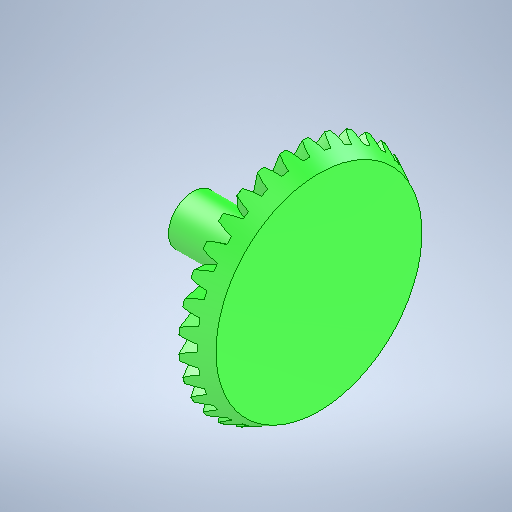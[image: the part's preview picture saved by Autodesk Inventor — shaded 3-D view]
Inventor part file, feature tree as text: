
AUTODESK INVENTOR PART (.ipt)
format: ipt  version: 2025.1 (Build 291241000, 241)  size: 666,624 bytes
history: native  units: in
note: dims shown in document units (in); Inventor stores cm internally (conversion verified against a paired STEP export)
features: sketch x8, extrude x5, plane x3, pattern_circular x3, revolve x1, hole x1, fillet x1, other x1
ambient origin geometry x8: Origin, YZ Plane, XZ Plane, XY Plane, X Axis, Y Axis, Z Axis, Center Point
bodies: Solid1 (feature_tree)
feature tree (23):
  revolve  "Revolution1"  [1 undecoded]
  plane  "Work Plane7"
  extrude  "Extrusion7"  Depth=0.0945in
  plane  "Work Plane8"
  sketch  "Sketch13"  dims[d5=0.3937in d9=1.5748in]
  extrude  "Extrusion9"  Depth=0.3937in
  pattern_circular  "Circular Pattern4"  [2 undecoded]
  pattern_circular  "Circular Pattern5"  [2 undecoded]
  extrude  "Extrusion10"  Depth=0.0394in
  extrude  "Extrusion11"  Depth=0.0394in
  extrude  "Extrusion12"  Depth=0.0394in
  pattern_circular  "Circular Pattern6"  [2 undecoded]
  hole  "Perçage1"  [1 undecoded]
  fillet  "Congé3"  Radius=0.0945in
  sketch  "Sketch1"  dims[d0=3.1496in d1=0.1825in]
  plane  "Work Plane6"
  sketch  "Sketch11"  dims[d2=0.0787in d3=0.0945in]
  sketch  "Sketch14"  dims[d10=90.0deg]
  sketch  "Sketch15"  dims[d74=0.4359in]
  sketch  "Sketch16"  dims[d75=0.7087in]
  sketch  "Sketch18"  dims[d76=0.9449in d77=1.4085in d78=0.7043in d86=-0.1825in d87=1.5748in d88=0.0691in d89=0.1374in d90=0.0787in d91=0.0197in d92=0.0945in d93=0.0079in d94=0.0079in d95=0.4724in d96=-0.0197in d109=0.2406in d110=-0.2406in d111=2.8171in d112=1.3386in d113=0.4724in d114=0.5906in d115=0.0in d116=2.3622in d117=360.0deg d119=12.5984in d120=360.0deg d122=1.1811in d123=0.0787in d124=0.0in d125=0.6142in d126=1.2598in d127=0.0in d128=0.1969in d129=0.7874in d130=0.2362in d131=0.0in d132=1.5748in d133=360.0deg d136=0.1181in d137=0.2362in d138=0.119in d139=0.0787in d140=0.5635in d141=0.2362in d142=0.8108in d143=0.1476in d144=0.0787in d145=0.7874in d147=360.0deg d149=0.0394in]
  sketch  "Esquisse19"
  other  "Réseau d'esquisse circulaire1"
note: 8 required parameter values undecoded (feature->parameter linkage not recoverable at this tier; creation-order binding heuristic only, values carry confidence <= 0.55)